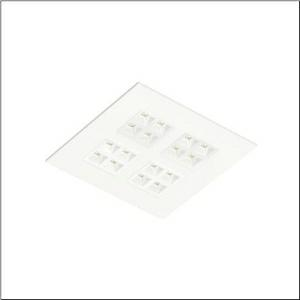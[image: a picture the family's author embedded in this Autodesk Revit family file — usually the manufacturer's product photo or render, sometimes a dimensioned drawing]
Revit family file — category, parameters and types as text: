
# Revit family: silica_r__31_square_51my6ndu44wa_4dbb
name_source: partatom
category: Lighting Fixtures
units: mm (PartAtom-declared; Revit-internal decimal feet)

## family parameters
Cut with Voids When Loaded = No
Host = Face
Light Source = No
Part Type = Normal
Room Calculation Point = No
Round Connector Dimension = Use Diameter
Shared = No

## types (1)
- --- (1 x LED, 6640 lm, 38.5 W, 4000K)
    Apparent Load = 39 VA
    CIE Flux Codes = 81 99 100 100 100
    Color Rendering = 80
    Color Temperature = 4000K
    Default Elevation = 1800 mm
    Description = Silica® 31 Square, office luminaire, primary light control with lens, of PMMA, primary anti-glare with reflector, of PC, white, light emission: direct distribution, primary light characteristic: symmetric, installation type: lay-in mounting, LED, rated luminous flux: 4.570lm, luminous efficacy: 176lm/W, light colour: 840, colour temperature: 4000K, control gear: DALI 2, Multilumen, with terminal, 5-pole, mains connection: 220..240V, AC, 50/60Hz, rated input power: 26W, luminaire housing, of sheet steel, coated, traffic white (RAL 9016), module: M625, length: 620mm, width: 620mm, height: 43mm, protection rating (complete): IP20, insulation class (complete): insulation class II (safety insulation), certification: CE, impact resistance: IK03, permissible operating ambient temperature: -20..+35°C, standard: EN 50419, packaging unit: 1 piece
    Height = 0 mm  [stored 0 ft]
    Lamp = 1 x LED
    Lamp Light Flux = 6640 lm
    Lamp Power = 38.5 W
    Lamp count = 1
    Length = 620 mm
    Luminous efficacy = 172 lm/W
    Manufacturer = Siteco
    ModVariant = No
    Model = 51MY6NDU44WA
    Mounting Place = Ceiling
    Mounting Type = Recessed
    Number of Poles = 1
    OnlyDefault = Yes
    Power Factor = 1
    Product Name = Silica® 31 Square
    Product group = office luminaire | ceiling recessed
    ProductGroupID = 401
    Protection Class = Protection class II
    Protection Degree = IP 20
    RLX_Detail_Level = 1
    RLX_Emergency_Light_Flux = 0 lm
    RLX_Emergency_Type = 0
    RLX_Emergency_Type_DB = No
    RlxData = <blob elided: 28065 chars, md5=272edaeb>
    Socket = socket
    Standby Power = 0 W
    System Light Flux = 6640 lm
    System Power = 39 W
    Type Comments = factory setting: luminous flux: 100 % | (OFF | OFF | OFF | OFF) | 1050 mA
    Type Image = l_1313651.jpg
    URL = http://relux.com
    VarID = @adj_036092
    Voltage = 0 V
    Weight = 0.00 kg
    Width = 620 mm

note: [stored X ft] marks values corroborated as IEEE doubles in the binary element streams (Revit-internal decimal feet)

## geometry (parser evidence)
native form markers: Blend x4, Sweep x10
no freeform markers — native parametric forms only
